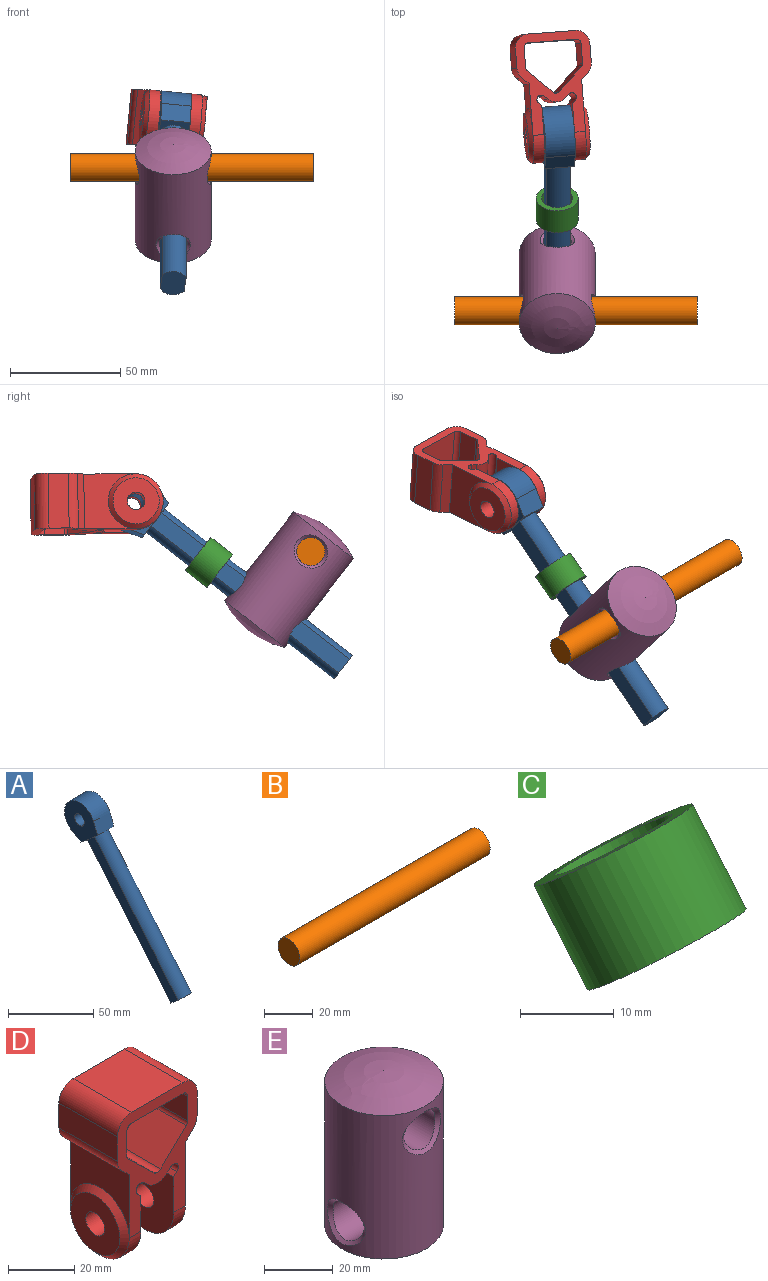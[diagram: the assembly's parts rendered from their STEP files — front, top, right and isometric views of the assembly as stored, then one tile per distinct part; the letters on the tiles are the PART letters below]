
ASSEMBLY  parts=5 mates=4
PART A: 12 faces, bbox 13.5x95.1x109.1 mm
  f0: plane 13.79x13.5mm, normal (0,-0.64,-0.77), area 113.2mm2, adj f2,f4,f5,f6,f7,f8,f9,f10
  f1: cylinder r=12.5mm len=24.13mm, axis (-1,0,0), area 639.1mm2, adj f2,f4,f5,f6
  f2: plane 13.5x8.37mm, normal (0,-0.93,0.37), area 121.5mm2, adj f0,f1,f5,f6
  f3: cylinder r=4mm len=13.5mm, axis (-1,0,0), area 339.3mm2, adj f5,f6
  f4: plane 13.5x7.67mm, normal (0,0.52,-0.85), area 121.5mm2, adj f0,f1,f5,f6
  f5: plane 27.86x27.43mm, normal (1,0,0), area 470.6mm2, adj f0,f1,f2,f3,f4
  f6: plane 27.86x27.43mm, normal (-1,0,0), area 470.6mm2, adj f0,f1,f2,f3,f4
  f7: plane 87.76x75.42mm, normal (-1,0,0), area 845.2mm2, adj f0,f8,f10,f11
  f8: cylinder r=6.75mm len=84.56mm, axis (0,0.64,0.77), area 1388.6mm2, adj f0,f7,f9,f11
  f9: plane 87.76x75.42mm, normal (1,0,0), area 845.2mm2, adj f0,f8,f10,f11
  f10: cylinder r=6.75mm len=84.56mm, axis (0,0.64,0.77), area 1388.6mm2, adj f0,f7,f9,f11
  f11: plane 11x10.34mm, normal (0,-0.64,-0.77), area 129.8mm2, adj f7,f8,f9,f10
PART B: 3 faces, bbox 110x12.7x12.7 mm
  f0: cylinder r=6.35mm len=110mm, axis (-1,0,0), area 4388.8mm2, adj f1,f2
  f1: plane 12.7x12.7mm, normal (1,0,0), area 126.7mm2, adj f0
  f2: plane 12.7x12.7mm, normal (-1,0,0), area 126.7mm2, adj f0
PART C: 4 faces, bbox 19x22.6x21.8 mm
  f0: cylinder r=9.5mm len=22.59mm, axis (0,0.64,0.77), area 746.1mm2, adj f2,f3
  f1: cylinder r=7mm len=18.76mm, axis (0,0.64,0.77), area 549.8mm2, adj f2,f3
  f2: plane 19x14.56mm, normal (0,-0.64,-0.77), area 129.6mm2, adj f0,f1
  f3: plane 19x14.56mm, normal (0,0.64,0.77), area 129.6mm2, adj f0,f1
PART D: 40 faces, bbox 34x25x58.5 mm
  f0: plane 25x23.5mm, normal (-1,0,0), area 342.2mm2, adj f4,f5,f10,f38
  f1: plane 25.68x25mm, normal (1,0,0), area 524.6mm2, adj f4,f5,f11,f33,f39
  f2: plane 25.68x25mm, normal (-1,0,0), area 524.6mm2, adj f4,f5,f17,f32,f34
  f3: plane 25x23.5mm, normal (1,0,0), area 342.2mm2, adj f4,f5,f18,f36
  f4: plane 46x34mm, normal (0,-1,0), area 582.1mm2, adj f0,f1,f2,f3,f6,f7,f8,f9
  f5: plane 46x34mm, normal (0,1,0), area 582.1mm2, adj f0,f1,f2,f3,f6,f7,f8,f9
  f6: plane 25x22mm, normal (0,0,1), area 550mm2, adj f4,f5,f7,f31
  f7: cylinder r=6mm len=25mm, axis (0,1,0), area 235.6mm2, adj f4,f5,f6,f8
  f8: plane 25x9.15mm, normal (-1,0,0), area 228.7mm2, adj f4,f5,f7,f9
  f9: cylinder r=6mm len=25mm, axis (0,1,0), area 121.1mm2, adj f4,f5,f8,f10
  f10: plane 25x3.15mm, normal (-0.69,0,-0.72), area 109mm2, adj f0,f4,f5,f9
  f11: plane 25x1.38mm, normal (0.69,0,0.72), area 47.9mm2, adj f1,f4,f5,f12
  f12: cylinder r=2mm len=25mm, axis (0,1,0), area 157.1mm2, adj f4,f5,f11,f13
  f13: plane 25x1.47mm, normal (-0.69,0,-0.72), area 50.8mm2, adj f4,f5,f12,f14
  f14: cylinder r=6mm len=25mm, axis (0,1,0), area 229.1mm2, adj f4,f5,f13,f15
  f15: plane 25x1.47mm, normal (0.69,0,-0.72), area 50.8mm2, adj f4,f5,f14,f16
  f16: cylinder r=2mm len=25mm, axis (0,1,0), area 157.1mm2, adj f4,f5,f15,f17
  f17: plane 25x1.38mm, normal (-0.69,0,0.72), area 47.9mm2, adj f2,f4,f5,f16
  f18: plane 25x3.15mm, normal (0.69,0,-0.72), area 109mm2, adj f3,f4,f5,f19
  f19: cylinder r=6mm len=25mm, axis (0,1,0), area 121.1mm2, adj f4,f5,f18,f20
  f20: plane 25x9.15mm, normal (1,0,0), area 228.7mm2, adj f4,f5,f19,f31
  f21: plane 25x22mm, normal (0,0,-1), area 550mm2, adj f4,f5,f22,f30
  f22: cylinder r=2mm len=25mm, axis (0,1,0), area 78.5mm2, adj f4,f5,f21,f23
  f23: plane 25x9.15mm, normal (-1,0,0), area 228.7mm2, adj f4,f5,f22,f24
  f24: cylinder r=2mm len=25mm, axis (0,1,0), area 40.4mm2, adj f4,f5,f23,f25
  f25: plane 25x11mm, normal (-0.69,0,0.72), area 380.8mm2, adj f4,f5,f24,f26
  f26: cylinder r=2mm len=25mm, axis (0,1,0), area 76.4mm2, adj f4,f5,f25,f27
  f27: plane 25x11mm, normal (0.69,0,0.72), area 380.8mm2, adj f4,f5,f26,f28
  f28: cylinder r=2mm len=25mm, axis (0,1,0), area 40.4mm2, adj f4,f5,f27,f29
  f29: plane 25x9.15mm, normal (1,0,0), area 228.7mm2, adj f4,f5,f28,f30
  f30: cylinder r=2mm len=25mm, axis (0,1,0), area 78.5mm2, adj f4,f5,f21,f29
  f31: cylinder r=6mm len=25mm, axis (0,1,0), area 235.6mm2, adj f4,f5,f6,f20
  f32: cylinder r=12.5mm len=25mm, axis (1,0,0), area 196.3mm2, adj f2,f4,f5,f36
  f33: cylinder r=12.5mm len=25mm, axis (1,0,0), area 196.3mm2, adj f1,f4,f5,f38
  f34: cylinder r=4mm len=8mm, axis (-1,0,0), area 175.9mm2, adj f2,f35
  f35: plane 21x21mm, normal (1,0,0), area 296.1mm2, adj f34,f36
  f36: cone r=10.5mm half-angle=45deg, axis (-1,0,0), area 204.4mm2, adj f3,f32,f35
  f37: plane 21x21mm, normal (-1,0,0), area 296.1mm2, adj f38,f39
  f38: cone r=12.5mm half-angle=45deg, axis (1,0,0), area 204.4mm2, adj f0,f33,f37
  f39: cylinder r=4mm len=8mm, axis (1,0,0), area 175.9mm2, adj f1,f37
PART E: 9 faces, bbox 34.5x34.5x59 mm
  f0: cylinder r=17.25mm len=51mm, axis (0,0,-1), area 4787.6mm2, adj f1,f2,f4,f5,f7,f8
  f1: sphere r=39.2mm, area 985.1mm2, adj f0
  f2: sphere r=39.2mm, area 985.1mm2, adj f0
  f3: cylinder r=6.35mm len=32.5mm, axis (0,-1,0), area 1296.7mm2, adj f4,f5
  f4: bspline ~15.6x14.68mm, area 69.4mm2, adj f0,f3
  f5: bspline ~15.6x14.68mm, area 69.4mm2, adj f0,f3
  f6: cylinder r=6.35mm len=32.5mm, axis (-1,0,0), area 1296.7mm2, adj f7,f8
  f7: bspline ~15.61x14.7mm, area 69.4mm2, adj f0,f6
  f8: bspline ~15.61x14.7mm, area 69.4mm2, adj f0,f6
PLACE A rot(axis=(-0.01,-0.72,-0.69),173deg) t=(-23.86,41.77,-4.96)mm
PLACE B t=(-16.51,28.01,-39.03)mm fixed
PLACE C rot(axis=(-0.01,-0.72,-0.69),173deg) t=(-23.86,22.48,-19.99)mm
PLACE D rot(axis=(-0.01,-0.71,-0.7),173deg) t=(-24.08,41.41,-4.93)mm
PLACE E rot(axis=(0,-0.95,-0.33),180deg) t=(-25.03,-29.1,-51.77)mm
MATE cylindrical B.f0 <-> E.f6  axis (-1,0,0) through (38.49,-39.03,-39.03)mm
MATE slider C.f0 <-> A.f8  axis (0,-0.79,-0.61) through (-25.03,2.27,-47.8)mm
MATE cylindrical E.f3 <-> C.f0  axis (0,-0.79,-0.61) through (-25.03,-6.21,-54.4)mm
MATE revolute D.f32 <-> A.f1  axis (-0.99,-0.08,0.1) through (-18.33,41.78,-18.04)mm
